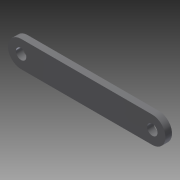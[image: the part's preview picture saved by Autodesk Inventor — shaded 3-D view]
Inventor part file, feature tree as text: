
AUTODESK INVENTOR PART (.ipt)
format: ipt  version: 2015 (Build 190159000, 159)  size: 95,744 bytes
history: native  units: mm
features: extrude x1, sketch x1
ambient origin geometry x8: Origin, YZ Plane, XZ Plane, XY Plane, X Axis, Y Axis, Z Axis, Center Point
bodies: Solid1 (feature_tree)
feature tree (2):
  extrude  "Extrusion1"  Depth=20.0mm
  sketch  "Sketch1"  dims[d0=100.0mm d1=20.0mm d2=8.0mm d3=8.0mm d4=5.0mm d5=0.0mm]
